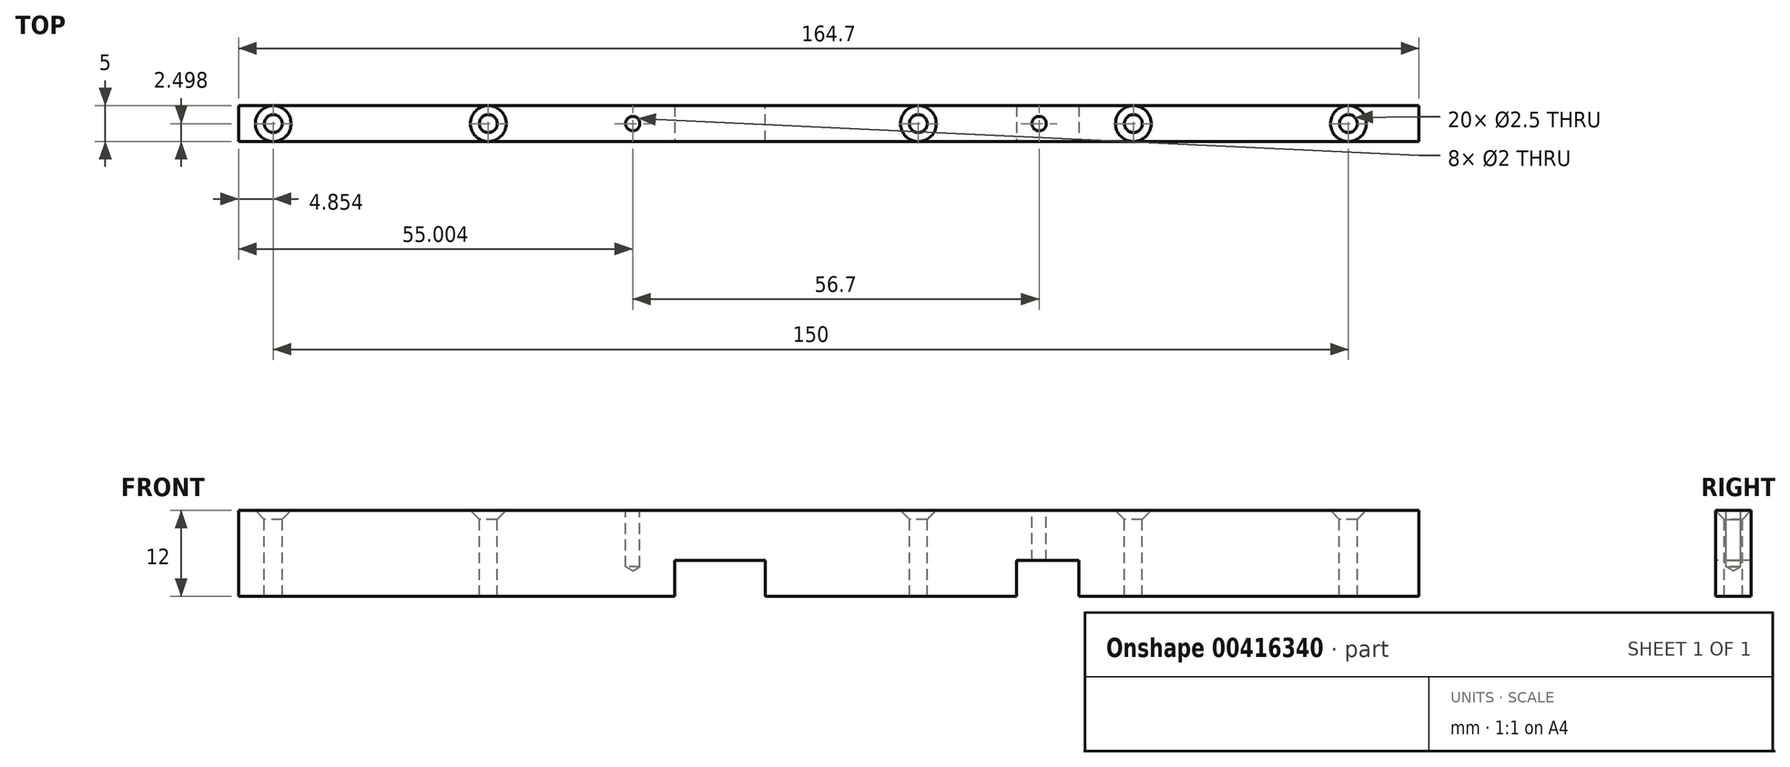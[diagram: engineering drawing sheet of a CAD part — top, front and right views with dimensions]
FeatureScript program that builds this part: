
annotation { "Feature Type Name" : "Feature", "Feature Type Description" : "" }
export const myFeature = defineFeature(function(context is Context, id is Id, definition is map)
    precondition{}
    {
        {
            var Q0;
            Q0=qCreatedBy(makeId("Top.planeOp"),FACE);
            var sketch = newSketch(context, id + "F0", { "sketchPlane" : qUnion([Q0])});
            skLineSegment(sketch, "E0", {"start": v(18.87, 90.14) * mm, "end": v(78.5, 90.14) * mm});
            skArc(sketch, "E1", {"start": v(18.87, 90.14) * mm, "mid": v(16.95, 89.76) * mm, "end": v(15.33, 88.67) * mm});
            skLineSegment(sketch, "E2", {"start": v(15.33, 88.67) * mm, "end": v(10.77, 84.1) * mm});
            skArc(sketch, "E3", {"start": v(10.77, 84.1) * mm, "mid": v(9.68, 82.49) * mm, "end": v(9.3, 80.57) * mm});
            skArc(sketch, "E4", {"start": v(15.33, 16.6) * mm, "mid": v(16.95, 15.52) * mm, "end": v(18.87, 15.14) * mm});
            skLineSegment(sketch, "E5", {"start": v(100.75, 15.14) * mm, "end": v(18.87, 15.14) * mm});
            skArc(sketch, "E6", {"start": v(100.75, 15.14) * mm, "mid": v(102.67, 15.52) * mm, "end": v(104.29, 16.6) * mm});
            skLineSegment(sketch, "E7", {"start": v(104.29, 16.6) * mm, "end": v(105.78, 18.1) * mm});
            skLineSegment(sketch, "E8", {"start": v(112.85, 18.1) * mm, "end": v(114.35, 16.6) * mm});
            skArc(sketch, "E9", {"start": v(114.35, 16.6) * mm, "mid": v(115.97, 15.52) * mm, "end": v(117.88, 15.14) * mm});
            skLineSegment(sketch, "E10", {"start": v(164.74, 15.14) * mm, "end": v(117.88, 15.14) * mm});
            skArc(sketch, "E11", {"start": v(164.74, 15.14) * mm, "mid": v(166.65, 15.52) * mm, "end": v(168.28, 16.6) * mm});
            skArc(sketch, "E12", {"start": v(172.84, 21.17) * mm, "mid": v(173.92, 22.79) * mm, "end": v(174.3, 24.7) * mm});
            skLineSegment(sketch, "E13", {"start": v(174.3, 80.57) * mm, "end": v(174.3, 24.7) * mm});
            skArc(sketch, "E14", {"start": v(174.3, 80.57) * mm, "mid": v(173.92, 82.49) * mm, "end": v(172.84, 84.1) * mm});
            skArc(sketch, "E15", {"start": v(168.28, 88.67) * mm, "mid": v(166.65, 89.76) * mm, "end": v(164.74, 90.14) * mm});
            skLineSegment(sketch, "E16", {"start": v(117.88, 90.14) * mm, "end": v(164.74, 90.14) * mm});
            skArc(sketch, "E17", {"start": v(117.88, 90.14) * mm, "mid": v(115.97, 89.76) * mm, "end": v(114.35, 88.67) * mm});
            skLineSegment(sketch, "E18", {"start": v(112.85, 87.18) * mm, "end": v(114.35, 88.67) * mm});
            skArc(sketch, "E19", {"start": v(105.78, 87.18) * mm, "mid": v(109.32, 85.72) * mm, "end": v(112.85, 87.18) * mm});
            skLineSegment(sketch, "E20", {"start": v(104.29, 88.67) * mm, "end": v(105.78, 87.18) * mm});
            skArc(sketch, "E21", {"start": v(104.29, 88.67) * mm, "mid": v(102.67, 89.76) * mm, "end": v(100.75, 90.14) * mm});
            skLineSegment(sketch, "E22", {"start": v(95.9, 90.14) * mm, "end": v(94.87, 91.17) * mm});
            skArc(sketch, "E23", {"start": v(91.33, 92.64) * mm, "mid": v(93.25, 92.26) * mm, "end": v(94.87, 91.17) * mm});
            skLineSegment(sketch, "E24", {"start": v(91.33, 92.64) * mm, "end": v(83.08, 92.64) * mm});
            skArc(sketch, "E25", {"start": v(79.54, 91.17) * mm, "mid": v(81.16, 92.26) * mm, "end": v(83.08, 92.64) * mm});
            skLineSegment(sketch, "E26", {"start": v(79.54, 91.17) * mm, "end": v(78.5, 90.14) * mm});
            skCircle(sketch, "E27", {"center": v(176.8, 54.89) * mm, "radius": 0.8 * mm});
            skCircle(sketch, "E28", {"center": v(176.8, 84.64) * mm, "radius": 0.8 * mm});
            skCircle(sketch, "E29", {"center": v(159.3, 12.64) * mm, "radius": 0.8 * mm});
            skCircle(sketch, "E30", {"center": v(176.8, 25.14) * mm, "radius": 0.8 * mm});
            skCircle(sketch, "E31", {"center": v(159.3, 92.64) * mm, "radius": 0.8 * mm});
            skCircle(sketch, "E32", {"center": v(119.3, 12.64) * mm, "radius": 0.8 * mm});
            skCircle(sketch, "E33", {"center": v(99.3, 12.64) * mm, "radius": 0.8 * mm});
            skCircle(sketch, "E34", {"center": v(59.3, 12.64) * mm, "radius": 0.8 * mm});
            skCircle(sketch, "E35", {"center": v(19.3, 12.64) * mm, "radius": 0.8 * mm});
            skCircle(sketch, "E36", {"center": v(119.3, 92.64) * mm, "radius": 0.8 * mm});
            skCircle(sketch, "E37", {"center": v(99.3, 92.64) * mm, "radius": 0.8 * mm});
            skCircle(sketch, "E38", {"center": v(6.8, 80.14) * mm, "radius": 0.8 * mm});
            skCircle(sketch, "E39", {"center": v(6.8, 53.84) * mm, "radius": 0.8 * mm});
            skCircle(sketch, "E40", {"center": v(59.3, 92.64) * mm, "radius": 0.8 * mm});
            skCircle(sketch, "E41", {"center": v(19.3, 92.64) * mm, "radius": 0.8 * mm});
            skLineSegment(sketch, "E42", {"start": v(4.3, 95.14) * mm, "end": v(179.3, 95.14) * mm});
            skLineSegment(sketch, "E43", {"start": v(179.3, 95.14) * mm, "end": v(179.3, 10.14) * mm});
            skLineSegment(sketch, "E44", {"start": v(179.3, 10.14) * mm, "end": v(4.3, 10.14) * mm});
            skCircle(sketch, "E45", {"center": v(9.3, 15.14) * mm, "radius": 2.15 * mm});
            skCircle(sketch, "E46", {"center": v(109.3, 15.14) * mm, "radius": 2.15 * mm});
            skCircle(sketch, "E47", {"center": v(9.3, 90.14) * mm, "radius": 2.15 * mm});
            skCircle(sketch, "E48", {"center": v(174.3, 90.14) * mm, "radius": 2.15 * mm});
            skCircle(sketch, "E49", {"center": v(174.3, 15.14) * mm, "radius": 2.15 * mm});
            skCircle(sketch, "E50", {"center": v(109.3, 90.14) * mm, "radius": 2.15 * mm});
            skLineSegment(sketch, "E51", {"start": v(95.9, 90.14) * mm, "end": v(100.75, 90.14) * mm});
            skArc(sketch, "E52", {"start": v(8.3, 25.7) * mm, "mid": v(8.68, 23.79) * mm, "end": v(9.77, 22.17) * mm});
            skArc(sketch, "E53", {"start": v(9.3, 49.78) * mm, "mid": v(8.56, 48.36) * mm, "end": v(8.3, 46.78) * mm});
            skLineSegment(sketch, "E54", {"start": v(9.3, 49.78) * mm, "end": v(9.3, 80.57) * mm});
            skLineSegment(sketch, "E55", {"start": v(15.33, 16.6) * mm, "end": v(9.77, 22.17) * mm});
            skLineSegment(sketch, "E56", {"start": v(8.3, 46.78) * mm, "end": v(8.3, 25.7) * mm});
            skLineSegment(sketch, "E57", {"start": v(168.28, 16.6) * mm, "end": v(172.84, 21.17) * mm});
            skLineSegment(sketch, "E58", {"start": v(4.3, 10.14) * mm, "end": v(4.3, 95.14) * mm});
            skLineSegment(sketch, "E59", {"start": v(168.28, 88.67) * mm, "end": v(172.84, 84.1) * mm});
            skLineSegment(sketch, "E60", {"start": v(9.3, 51.64) * mm, "end": v(9.8, 51.64) * mm});
            skLineSegment(sketch, "E61", {"start": v(9.8, 51.24) * mm, "end": v(9.3, 51.24) * mm});
            skLineSegment(sketch, "E62", {"start": v(9.34, 22.66) * mm, "end": v(9.8, 22.66) * mm});
            skArc(sketch, "E63", {"start": v(9.8, 23.9) * mm, "mid": v(11.41, 22.85) * mm, "end": v(13.3, 22.48) * mm});
            skLineSegment(sketch, "E64", {"start": v(13.3, 22.48) * mm, "end": v(124.3, 22.48) * mm});
            skArc(sketch, "E65", {"start": v(124.3, 22.48) * mm, "mid": v(127.84, 23.94) * mm, "end": v(129.3, 27.48) * mm});
            skLineSegment(sketch, "E66", {"start": v(129.3, 27.48) * mm, "end": v(129.3, 46.78) * mm});
            skArc(sketch, "E67", {"start": v(129.3, 46.78) * mm, "mid": v(127.84, 50.31) * mm, "end": v(124.3, 51.78) * mm});
            skLineSegment(sketch, "E68", {"start": v(13.3, 51.78) * mm, "end": v(124.3, 51.78) * mm});
            skArc(sketch, "E69", {"start": v(13.3, 51.78) * mm, "mid": v(11.41, 51.4) * mm, "end": v(9.8, 50.35) * mm});
            skLineSegment(sketch, "E70", {"start": v(9.8, 50.35) * mm, "end": v(9.8, 51.64) * mm});
            skLineSegment(sketch, "E71", {"start": v(9.8, 22.26) * mm, "end": v(9.8, 23.9) * mm});
            skLineSegment(sketch, "E72", {"start": v(36.43, 70.73) * mm, "end": v(36.43, 66.15) * mm});
            skLineSegment(sketch, "E73", {"start": v(36.43, 66.15) * mm, "end": v(23.24, 66.15) * mm});
            skArc(sketch, "E74", {"start": v(23.24, 66.15) * mm, "mid": v(18.24, 61.15) * mm, "end": v(23.24, 56.15) * mm});
            skLineSegment(sketch, "E75", {"start": v(63.42, 56.15) * mm, "end": v(23.24, 56.15) * mm});
            skArc(sketch, "E76", {"start": v(63.42, 56.15) * mm, "mid": v(66.95, 57.6) * mm, "end": v(68.42, 61.15) * mm});
            skLineSegment(sketch, "E77", {"start": v(68.42, 62.67) * mm, "end": v(68.42, 61.15) * mm});
            skArc(sketch, "E78", {"start": v(68.42, 62.67) * mm, "mid": v(66.95, 66.2) * mm, "end": v(63.42, 67.67) * mm});
            skLineSegment(sketch, "E79", {"start": v(58.94, 67.67) * mm, "end": v(63.42, 67.67) * mm});
            skLineSegment(sketch, "E80", {"start": v(58.94, 70.73) * mm, "end": v(58.94, 67.67) * mm});
            skArc(sketch, "E81", {"start": v(58.94, 70.73) * mm, "mid": v(57.47, 74.27) * mm, "end": v(53.94, 75.73) * mm});
            skLineSegment(sketch, "E82", {"start": v(41.43, 75.73) * mm, "end": v(53.94, 75.73) * mm});
            skArc(sketch, "E83", {"start": v(41.43, 75.73) * mm, "mid": v(37.9, 74.27) * mm, "end": v(36.43, 70.73) * mm});
            skCircle(sketch, "E84", {"center": v(20.67, 88.22) * mm, "radius": 1.5 * mm});
            skCircle(sketch, "E85", {"center": v(43.43, 88.22) * mm, "radius": 1.5 * mm});
            skCircle(sketch, "E86", {"center": v(87.18, 87.32) * mm, "radius": 1.02 * mm});
            skCircle(sketch, "E87", {"center": v(87.19, 66.74) * mm, "radius": 1.02 * mm});
            skCircle(sketch, "E88", {"center": v(12.43, 67.14) * mm, "radius": 0.8 * mm});
            skCircle(sketch, "E89", {"center": v(24.3, 72.14) * mm, "radius": 0.8 * mm});
            skCircle(sketch, "E90", {"center": v(25.95, 86.94) * mm, "radius": 0.8 * mm});
            skCircle(sketch, "E91", {"center": v(56.3, 87.03) * mm, "radius": 0.8 * mm});
            skCircle(sketch, "E92", {"center": v(61.25, 73.02) * mm, "radius": 0.8 * mm});
            skCircle(sketch, "E93", {"center": v(77.3, 87.03) * mm, "radius": 0.8 * mm});
            skCircle(sketch, "E94", {"center": v(103.58, 71.9) * mm, "radius": 0.8 * mm});
            skCircle(sketch, "E95", {"center": v(95.44, 87.66) * mm, "radius": 0.8 * mm});
            skCircle(sketch, "E96", {"center": v(112.81, 82.14) * mm, "radius": 0.8 * mm});
            skCircle(sketch, "E97", {"center": v(132.3, 71.14) * mm, "radius": 0.8 * mm});
            skCircle(sketch, "E98", {"center": v(131.08, 84.74) * mm, "radius": 0.8 * mm});
            skCircle(sketch, "E99", {"center": v(148.41, 39.7) * mm, "radius": 0.8 * mm});
            skCircle(sketch, "E100", {"center": v(170.3, 28.14) * mm, "radius": 0.8 * mm});
            skCircle(sketch, "E101", {"center": v(169.46, 82.57) * mm, "radius": 0.8 * mm});
            skCircle(sketch, "E102", {"center": v(171.43, 70.95) * mm, "radius": 0.8 * mm});
            skCircle(sketch, "E103", {"center": v(79.53, 66.84) * mm, "radius": 0.8 * mm});
            skCircle(sketch, "E104", {"center": v(158.16, 71.12) * mm, "radius": 0.8 * mm});
            skCircle(sketch, "E105", {"center": v(158.22, 82.82) * mm, "radius": 0.8 * mm});
            skLineSegment(sketch, "E106", {"start": v(153.8, 58.09) * mm, "end": v(137, 58.09) * mm});
            skArc(sketch, "E107", {"start": v(155.3, 59.59) * mm, "mid": v(154.86, 58.53) * mm, "end": v(153.8, 58.09) * mm});
            skLineSegment(sketch, "E108", {"start": v(155.3, 83.2) * mm, "end": v(155.3, 59.59) * mm});
            skArc(sketch, "E109", {"start": v(153.8, 84.7) * mm, "mid": v(154.86, 84.25) * mm, "end": v(155.3, 83.2) * mm});
            skLineSegment(sketch, "E110", {"start": v(137, 84.7) * mm, "end": v(153.8, 84.7) * mm});
            skArc(sketch, "E111", {"start": v(135.5, 83.2) * mm, "mid": v(135.93, 84.25) * mm, "end": v(137, 84.7) * mm});
            skLineSegment(sketch, "E112", {"start": v(135.5, 59.59) * mm, "end": v(135.5, 83.2) * mm});
            skArc(sketch, "E113", {"start": v(137, 58.09) * mm, "mid": v(135.93, 58.53) * mm, "end": v(135.5, 59.59) * mm});
            skArc(sketch, "E114", {"start": v(9.8, 23.9) * mm, "mid": v(8.7, 25.54) * mm, "end": v(8.3, 27.48) * mm});
            skArc(sketch, "E115", {"start": v(9.3, 49.78) * mm, "mid": v(9.54, 50.07) * mm, "end": v(9.8, 50.35) * mm});
            skLineSegment(sketch, "E116", {"start": v(18.3, 27.48) * mm, "end": v(18.3, 46.78) * mm});
            skArc(sketch, "E117", {"start": v(13.3, 22.48) * mm, "mid": v(16.84, 23.94) * mm, "end": v(18.3, 27.48) * mm});
            skArc(sketch, "E118", {"start": v(18.3, 46.78) * mm, "mid": v(16.84, 50.31) * mm, "end": v(13.3, 51.78) * mm});
            skCircle(sketch, "E119", {"center": v(152.55, 66.64) * mm, "radius": 0.6 * mm});
            skCircle(sketch, "E120", {"center": v(152.55, 81.14) * mm, "radius": 0.6 * mm});
            skCircle(sketch, "E121", {"center": v(138.05, 66.64) * mm, "radius": 0.6 * mm});
            skCircle(sketch, "E122", {"center": v(138.05, 81.14) * mm, "radius": 0.6 * mm});
            skCircle(sketch, "E123", {"center": v(19.3, 92.64) * mm, "radius": 0.78 * mm});
            skArc(sketch, "E124", {"start": v(19.1, 91.66) * mm, "mid": v(20.02, 93.33) * mm, "end": v(18.32, 92.47) * mm});
            skCircle(sketch, "E125", {"center": v(25.95, 86.94) * mm, "radius": 0.78 * mm});
            skArc(sketch, "E126", {"start": v(25.76, 85.96) * mm, "mid": v(26.67, 87.63) * mm, "end": v(24.97, 86.77) * mm});
            skCircle(sketch, "E127", {"center": v(6.8, 80.14) * mm, "radius": 0.78 * mm});
            skArc(sketch, "E128", {"start": v(6.6, 79.16) * mm, "mid": v(7.52, 80.83) * mm, "end": v(5.82, 79.97) * mm});
            skCircle(sketch, "E129", {"center": v(24.3, 72.14) * mm, "radius": 0.78 * mm});
            skArc(sketch, "E130", {"start": v(24.1, 71.16) * mm, "mid": v(25.02, 72.83) * mm, "end": v(23.32, 71.97) * mm});
            skCircle(sketch, "E131", {"center": v(12.43, 67.14) * mm, "radius": 0.78 * mm});
            skArc(sketch, "E132", {"start": v(12.23, 66.16) * mm, "mid": v(13.14, 67.83) * mm, "end": v(11.44, 66.97) * mm});
            skCircle(sketch, "E133", {"center": v(59.3, 92.64) * mm, "radius": 0.78 * mm});
            skArc(sketch, "E134", {"start": v(59.1, 91.66) * mm, "mid": v(60.02, 93.33) * mm, "end": v(58.32, 92.47) * mm});
            skCircle(sketch, "E135", {"center": v(56.3, 87.03) * mm, "radius": 0.78 * mm});
            skArc(sketch, "E136", {"start": v(56.1, 86.05) * mm, "mid": v(57.02, 87.73) * mm, "end": v(55.32, 86.87) * mm});
            skCircle(sketch, "E137", {"center": v(77.3, 87.03) * mm, "radius": 0.78 * mm});
            skArc(sketch, "E138", {"start": v(77.1, 86.05) * mm, "mid": v(78.02, 87.73) * mm, "end": v(76.32, 86.87) * mm});
            skCircle(sketch, "E139", {"center": v(61.25, 73.02) * mm, "radius": 0.78 * mm});
            skArc(sketch, "E140", {"start": v(61.06, 72.04) * mm, "mid": v(61.97, 73.71) * mm, "end": v(60.27, 72.85) * mm});
            skCircle(sketch, "E141", {"center": v(99.3, 92.64) * mm, "radius": 0.78 * mm});
            skArc(sketch, "E142", {"start": v(99.1, 91.66) * mm, "mid": v(100.02, 93.33) * mm, "end": v(98.32, 92.47) * mm});
            skCircle(sketch, "E143", {"center": v(95.44, 87.66) * mm, "radius": 0.78 * mm});
            skArc(sketch, "E144", {"start": v(95.25, 86.68) * mm, "mid": v(96.16, 88.36) * mm, "end": v(94.46, 87.5) * mm});
            skCircle(sketch, "E145", {"center": v(103.58, 71.9) * mm, "radius": 0.78 * mm});
            skArc(sketch, "E146", {"start": v(103.39, 70.92) * mm, "mid": v(104.3, 72.6) * mm, "end": v(102.6, 71.73) * mm});
            skCircle(sketch, "E147", {"center": v(79.53, 66.84) * mm, "radius": 0.78 * mm});
            skArc(sketch, "E148", {"start": v(79.33, 65.86) * mm, "mid": v(80.25, 67.54) * mm, "end": v(78.54, 66.68) * mm});
            skCircle(sketch, "E149", {"center": v(119.3, 92.64) * mm, "radius": 0.78 * mm});
            skArc(sketch, "E150", {"start": v(119.1, 91.66) * mm, "mid": v(120.02, 93.33) * mm, "end": v(118.32, 92.47) * mm});
            skCircle(sketch, "E151", {"center": v(131.08, 84.74) * mm, "radius": 0.78 * mm});
            skArc(sketch, "E152", {"start": v(130.89, 83.76) * mm, "mid": v(131.8, 85.43) * mm, "end": v(130.1, 84.57) * mm});
            skCircle(sketch, "E153", {"center": v(132.3, 71.14) * mm, "radius": 0.78 * mm});
            skArc(sketch, "E154", {"start": v(132.1, 70.16) * mm, "mid": v(133.02, 71.83) * mm, "end": v(131.32, 70.97) * mm});
            skCircle(sketch, "E155", {"center": v(159.3, 92.64) * mm, "radius": 0.78 * mm});
            skArc(sketch, "E156", {"start": v(159.1, 91.66) * mm, "mid": v(160.02, 93.33) * mm, "end": v(158.32, 92.47) * mm});
            skCircle(sketch, "E157", {"center": v(158.22, 82.82) * mm, "radius": 0.78 * mm});
            skArc(sketch, "E158", {"start": v(158.03, 81.84) * mm, "mid": v(158.94, 83.51) * mm, "end": v(157.24, 82.65) * mm});
            skCircle(sketch, "E159", {"center": v(158.16, 71.12) * mm, "radius": 0.78 * mm});
            skArc(sketch, "E160", {"start": v(157.97, 70.14) * mm, "mid": v(158.88, 71.81) * mm, "end": v(157.18, 70.95) * mm});
            skCircle(sketch, "E161", {"center": v(169.46, 82.57) * mm, "radius": 0.78 * mm});
            skArc(sketch, "E162", {"start": v(169.27, 81.59) * mm, "mid": v(170.18, 83.26) * mm, "end": v(168.48, 82.4) * mm});
            skCircle(sketch, "E163", {"center": v(171.43, 70.95) * mm, "radius": 0.78 * mm});
            skArc(sketch, "E164", {"start": v(171.24, 69.97) * mm, "mid": v(172.15, 71.64) * mm, "end": v(170.45, 70.78) * mm});
            skCircle(sketch, "E165", {"center": v(176.8, 84.64) * mm, "radius": 0.78 * mm});
            skArc(sketch, "E166", {"start": v(176.6, 83.66) * mm, "mid": v(177.52, 85.33) * mm, "end": v(175.82, 84.47) * mm});
            skCircle(sketch, "E167", {"center": v(176.8, 54.89) * mm, "radius": 0.78 * mm});
            skArc(sketch, "E168", {"start": v(176.6, 53.9) * mm, "mid": v(177.52, 55.58) * mm, "end": v(175.82, 54.72) * mm});
            skCircle(sketch, "E169", {"center": v(176.8, 25.14) * mm, "radius": 0.78 * mm});
            skArc(sketch, "E170", {"start": v(176.6, 24.16) * mm, "mid": v(177.52, 25.83) * mm, "end": v(175.82, 24.97) * mm});
            skCircle(sketch, "E171", {"center": v(170.3, 28.14) * mm, "radius": 0.78 * mm});
            skArc(sketch, "E172", {"start": v(170.1, 27.16) * mm, "mid": v(171.02, 28.83) * mm, "end": v(169.32, 27.97) * mm});
            skCircle(sketch, "E173", {"center": v(148.41, 39.7) * mm, "radius": 0.78 * mm});
            skArc(sketch, "E174", {"start": v(148.22, 38.71) * mm, "mid": v(149.13, 40.4) * mm, "end": v(147.43, 39.53) * mm});
            skCircle(sketch, "E175", {"center": v(159.3, 12.64) * mm, "radius": 0.78 * mm});
            skArc(sketch, "E176", {"start": v(159.1, 11.66) * mm, "mid": v(160.02, 13.33) * mm, "end": v(158.32, 12.47) * mm});
            skCircle(sketch, "E177", {"center": v(164.3, 53.64) * mm, "radius": 0.78 * mm});
            skCircle(sketch, "E178", {"center": v(134.3, 53.64) * mm, "radius": 0.78 * mm});
            skCircle(sketch, "E179", {"center": v(104.3, 53.64) * mm, "radius": 0.78 * mm});
            skCircle(sketch, "E180", {"center": v(99.3, 12.64) * mm, "radius": 0.78 * mm});
            skArc(sketch, "E181", {"start": v(99.1, 11.66) * mm, "mid": v(100.02, 13.33) * mm, "end": v(98.32, 12.47) * mm});
            skCircle(sketch, "E182", {"center": v(119.3, 12.64) * mm, "radius": 0.78 * mm});
            skArc(sketch, "E183", {"start": v(119.1, 11.66) * mm, "mid": v(120.02, 13.33) * mm, "end": v(118.32, 12.47) * mm});
            skCircle(sketch, "E184", {"center": v(74.3, 53.64) * mm, "radius": 0.78 * mm});
            skCircle(sketch, "E185", {"center": v(59.3, 12.64) * mm, "radius": 0.78 * mm});
            skArc(sketch, "E186", {"start": v(59.1, 11.66) * mm, "mid": v(60.02, 13.33) * mm, "end": v(58.32, 12.47) * mm});
            skCircle(sketch, "E187", {"center": v(19.3, 12.64) * mm, "radius": 0.78 * mm});
            skArc(sketch, "E188", {"start": v(19.1, 11.66) * mm, "mid": v(20.02, 13.33) * mm, "end": v(18.32, 12.47) * mm});
            skCircle(sketch, "E189", {"center": v(6.8, 53.84) * mm, "radius": 0.78 * mm});
            skArc(sketch, "E190", {"start": v(6.6, 52.86) * mm, "mid": v(7.52, 54.53) * mm, "end": v(5.82, 53.67) * mm});
            skCircle(sketch, "E191", {"center": v(14.3, 53.64) * mm, "radius": 0.78 * mm});
            skCircle(sketch, "E192", {"center": v(44.3, 53.64) * mm, "radius": 0.78 * mm});
            skArc(sketch, "E193", {"start": v(86.86, 86.1) * mm, "mid": v(88.07, 88.2) * mm, "end": v(85.98, 87) * mm});
            skArc(sketch, "E194", {"start": v(86.86, 65.53) * mm, "mid": v(88.07, 67.63) * mm, "end": v(85.98, 66.42) * mm});
            skCircle(sketch, "E195", {"center": v(138.05, 81.14) * mm, "radius": 1.02 * mm});
            skArc(sketch, "E196", {"start": v(137.72, 79.93) * mm, "mid": v(138.93, 82.02) * mm, "end": v(136.84, 80.81) * mm});
            skCircle(sketch, "E197", {"center": v(152.55, 81.14) * mm, "radius": 1.02 * mm});
            skArc(sketch, "E198", {"start": v(152.22, 79.93) * mm, "mid": v(153.43, 82.02) * mm, "end": v(151.34, 80.81) * mm});
            skCircle(sketch, "E199", {"center": v(152.55, 66.64) * mm, "radius": 1.02 * mm});
            skArc(sketch, "E200", {"start": v(152.22, 65.43) * mm, "mid": v(153.43, 67.52) * mm, "end": v(151.34, 66.31) * mm});
            skCircle(sketch, "E201", {"center": v(138.05, 66.64) * mm, "radius": 1.02 * mm});
            skArc(sketch, "E202", {"start": v(137.72, 65.43) * mm, "mid": v(138.93, 67.52) * mm, "end": v(136.84, 66.31) * mm});
            skArc(sketch, "E203", {"start": v(112.62, 81.16) * mm, "mid": v(113.53, 82.83) * mm, "end": v(111.83, 81.97) * mm});
            skLineSegment(sketch, "E204", {"start": v(9.45, 51.14) * mm, "end": v(9.45, 56.14) * mm});
            skLineSegment(sketch, "E205", {"start": v(9.45, 56.14) * mm, "end": v(70.3, 56.14) * mm});
            skLineSegment(sketch, "E206", {"start": v(70.3, 56.14) * mm, "end": v(70.3, 51.14) * mm});
            skLineSegment(sketch, "E207", {"start": v(70.3, 51.14) * mm, "end": v(9.45, 51.14) * mm});
            skLineSegment(sketch, "E208", {"start": v(82.98, 51.14) * mm, "end": v(82.98, 56.14) * mm});
            skLineSegment(sketch, "E209", {"start": v(82.98, 56.14) * mm, "end": v(117.98, 56.14) * mm});
            skLineSegment(sketch, "E210", {"start": v(117.98, 56.14) * mm, "end": v(117.98, 51.14) * mm});
            skLineSegment(sketch, "E211", {"start": v(117.98, 51.14) * mm, "end": v(82.98, 51.14) * mm});
            skLineSegment(sketch, "E212", {"start": v(174.15, 51.14) * mm, "end": v(174.15, 56.14) * mm});
            skLineSegment(sketch, "E213", {"start": v(174.15, 56.14) * mm, "end": v(126.7, 56.14) * mm});
            skLineSegment(sketch, "E214", {"start": v(126.7, 56.14) * mm, "end": v(126.7, 51.14) * mm});
            skLineSegment(sketch, "E215", {"start": v(126.7, 51.14) * mm, "end": v(174.15, 51.14) * mm});
            skLineSegment(sketch, "E216", {"start": v(70.3, 51.14) * mm, "end": v(82.98, 51.14) * mm});
            skLineSegment(sketch, "E217", {"start": v(82.98, 56.14) * mm, "end": v(70.3, 56.14) * mm});
            skLineSegment(sketch, "E218", {"start": v(126.7, 51.14) * mm, "end": v(126.7, 56.14) * mm});
            skLineSegment(sketch, "E219", {"start": v(126.7, 56.14) * mm, "end": v(117.98, 56.14) * mm});
            skLineSegment(sketch, "E220", {"start": v(117.98, 51.14) * mm, "end": v(126.7, 51.14) * mm});
            skSolve(sketch);
        }
        {
            var Q0;
            Q0=makeQuery(id+"F0.imprint","IMPRINT",FACE,{"disambiguationData":[TD([[makeQuery(id+"F0.imprint","IMPRINT",EDGE,{"derivedFrom":sQuery(id+"F0.wireOp",EDGE,"E191")}),1.0]])]});
            var Q1;
            {var subQ1=sQuery(id+"F0.wireOp",EDGE,"E69");var subQ3=sQuery(id+"F0.wireOp",EDGE,"E207");var subQ4=makeQuery(id+"F0.imprint","INTERSECT",VERTEX,{"derivedFrom":[subQ1,subQ3]});Q1=makeQuery(id+"F0.imprint","IMPRINT",FACE,{"disambiguationData":[TD([[makeQuery(id+"F0.imprint","IMPRINT",EDGE,{"disambiguationData":[TD([[subQ4,1.0]])],"derivedFrom":subQ3}),-1.0]])]});}
            var Q2;
            {var subQ1=sQuery(id+"F0.wireOp",EDGE,"E68");var subQ3=sQuery(id+"F0.wireOp",EDGE,"E206");var subQ4=makeQuery(id+"F0.imprint","INTERSECT",VERTEX,{"derivedFrom":[subQ1,subQ3]});Q2=makeQuery(id+"F0.imprint","IMPRINT",FACE,{"disambiguationData":[TD([[makeQuery(id+"F0.imprint","IMPRINT",EDGE,{"disambiguationData":[TD([[subQ4,1.0]])],"derivedFrom":subQ1}),-1.0]])]});}
            var Q3;
            {var subQ0=sQuery(id+"F0.wireOp",EDGE,"E70");var subQ1=sQuery(id+"F0.wireOp",EDGE,"E60");var subQ2=makeQuery(id+"F0.imprint","INTERSECT",VERTEX,{"derivedFrom":[subQ1,subQ0]});Q3=makeQuery(id+"F0.imprint","IMPRINT",FACE,{"disambiguationData":[TD([[makeQuery(id+"F0.imprint","IMPRINT",EDGE,{"disambiguationData":[TD([[subQ2,1.0]])],"derivedFrom":subQ1}),-1.0]])]});}
            var Q4;
            {var subQ0=sQuery(id+"F0.wireOp",EDGE,"E70");var subQ1=sQuery(id+"F0.wireOp",EDGE,"E61");var subQ2=makeQuery(id+"F0.imprint","INTERSECT",VERTEX,{"derivedFrom":[subQ1,subQ0]});Q4=makeQuery(id+"F0.imprint","IMPRINT",FACE,{"disambiguationData":[TD([[makeQuery(id+"F0.imprint","IMPRINT",EDGE,{"disambiguationData":[TD([[subQ2,-1.0]])],"derivedFrom":subQ1}),1.0]])]});}
            var Q5;
            Q5=makeQuery(id+"F0.imprint","IMPRINT",FACE,{"disambiguationData":[TD([[makeQuery(id+"F0.imprint","IMPRINT",EDGE,{"derivedFrom":sQuery(id+"F0.wireOp",EDGE,"E179")}),1.0]])]});
            var Q6;
            {var subQ5=sQuery(id+"F0.wireOp",EDGE,"E216");Q6=makeQuery(id+"F0.imprint","IMPRINT",FACE,{"disambiguationData":[TD([[makeQuery(id+"F0.imprint","IMPRINT",EDGE,{"derivedFrom":subQ5}),1.0]])]});}
            var Q7;
            {var subQ5=sQuery(id+"F0.wireOp",EDGE,"E211");Q7=makeQuery(id+"F0.imprint","IMPRINT",FACE,{"disambiguationData":[TD([[makeQuery(id+"F0.imprint","IMPRINT",EDGE,{"derivedFrom":subQ5}),-1.0]])]});}
            var Q8;
            Q8=makeQuery(id+"F0.imprint","IMPRINT",FACE,{"disambiguationData":[TD([[makeQuery(id+"F0.imprint","IMPRINT",EDGE,{"derivedFrom":sQuery(id+"F0.wireOp",EDGE,"E177")}),1.0]])]});
            var Q9;
            {var subQ0=sQuery(id+"F0.wireOp",EDGE,"E215");var subQ1=sQuery(id+"F0.wireOp",EDGE,"E67");var subQ2=makeQuery(id+"F0.imprint","INTERSECT",VERTEX,{"derivedFrom":[subQ1,subQ0]});Q9=makeQuery(id+"F0.imprint","IMPRINT",FACE,{"disambiguationData":[TD([[makeQuery(id+"F0.imprint","IMPRINT",EDGE,{"disambiguationData":[TD([[subQ2,-1.0]])],"derivedFrom":subQ1}),1.0]])]});}
            var Q10;
            {var subQ0=sQuery(id+"F0.wireOp",EDGE,"E220");Q10=makeQuery(id+"F0.imprint","IMPRINT",FACE,{"disambiguationData":[TD([[makeQuery(id+"F0.imprint","IMPRINT",EDGE,{"derivedFrom":subQ0}),1.0]])]});}
            var Q11;
            Q11=makeQuery(id+"F0.imprint","IMPRINT",FACE,{"disambiguationData":[TD([[makeQuery(id+"F0.imprint","IMPRINT",EDGE,{"derivedFrom":sQuery(id+"F0.wireOp",EDGE,"E184")}),1.0]])]});
            var Q12;
            {var subQ0=sQuery(id+"F0.wireOp",EDGE,"E219");Q12=makeQuery(id+"F0.imprint","IMPRINT",FACE,{"disambiguationData":[TD([[makeQuery(id+"F0.imprint","IMPRINT",EDGE,{"derivedFrom":subQ0}),1.0]])]});}
            var Q13;
            Q13=makeQuery(id+"F0.imprint","IMPRINT",FACE,{"disambiguationData":[TD([[makeQuery(id+"F0.imprint","IMPRINT",EDGE,{"derivedFrom":sQuery(id+"F0.wireOp",EDGE,"E191")}),-1.0]])]});
            var Q14;
            Q14=makeQuery(id+"F0.imprint","IMPRINT",FACE,{"disambiguationData":[TD([[makeQuery(id+"F0.imprint","IMPRINT",EDGE,{"derivedFrom":sQuery(id+"F0.wireOp",EDGE,"E192")}),-1.0]])]});
            var Q15;
            Q15=makeQuery(id+"F0.imprint","IMPRINT",FACE,{"disambiguationData":[TD([[makeQuery(id+"F0.imprint","IMPRINT",EDGE,{"derivedFrom":sQuery(id+"F0.wireOp",EDGE,"E184")}),-1.0]])]});
            var Q16;
            Q16=makeQuery(id+"F0.imprint","IMPRINT",FACE,{"disambiguationData":[TD([[makeQuery(id+"F0.imprint","IMPRINT",EDGE,{"derivedFrom":sQuery(id+"F0.wireOp",EDGE,"E179")}),-1.0]])]});
            var Q17;
            Q17=makeQuery(id+"F0.imprint","IMPRINT",FACE,{"disambiguationData":[TD([[makeQuery(id+"F0.imprint","IMPRINT",EDGE,{"derivedFrom":sQuery(id+"F0.wireOp",EDGE,"E178")}),-1.0]])]});
            var Q18;
            Q18=makeQuery(id+"F0.imprint","IMPRINT",FACE,{"disambiguationData":[TD([[makeQuery(id+"F0.imprint","IMPRINT",EDGE,{"derivedFrom":sQuery(id+"F0.wireOp",EDGE,"E177")}),-1.0]])]});
            extrude(context, id + "F1", {"entities" : qUnion([Q0, Q1, Q2, Q3, Q4, Q5, Q6, Q7, Q8, Q9, Q10, Q11, Q12, Q13, Q14, Q15, Q16, Q17, Q18]), "depth" : 12 * mm, "offsetDistance" : 25 * mm});
        }
        {
            var Q0;
            Q0=makeQuery(id+"F1.opExtrude","CAP_FACE",FACE,{"disambiguationData":[OSD([sQuery(id+"F0.wireOp",EDGE,"E177"),sQuery(id+"F0.wireOp",EDGE,"E178"),sQuery(id+"F0.wireOp",EDGE,"E179"),sQuery(id+"F0.wireOp",EDGE,"E184"),sQuery(id+"F0.wireOp",EDGE,"E191"),sQuery(id+"F0.wireOp",EDGE,"E192"),sQuery(id+"F0.wireOp",EDGE,"E204"),sQuery(id+"F0.wireOp",EDGE,"E205"),sQuery(id+"F0.wireOp",EDGE,"E207"),sQuery(id+"F0.wireOp",EDGE,"E209"),sQuery(id+"F0.wireOp",EDGE,"E211"),sQuery(id+"F0.wireOp",EDGE,"E212"),sQuery(id+"F0.wireOp",EDGE,"E213"),sQuery(id+"F0.wireOp",EDGE,"E215"),sQuery(id+"F0.wireOp",EDGE,"E216"),sQuery(id+"F0.wireOp",EDGE,"E217"),sQuery(id+"F0.wireOp",EDGE,"E219"),sQuery(id+"F0.wireOp",EDGE,"E220")])],"isStart":false});
            var sketch = newSketch(context, id + "F2", { "sketchPlane" : qUnion([Q0])});
            skLineSegment(sketch, "E221", {"start": v(18.87, 90.14) * mm, "end": v(78.5, 90.14) * mm});
            skArc(sketch, "E222", {"start": v(18.87, 90.14) * mm, "mid": v(16.95, 89.76) * mm, "end": v(15.33, 88.67) * mm});
            skLineSegment(sketch, "E223", {"start": v(15.33, 88.67) * mm, "end": v(10.77, 84.1) * mm});
            skArc(sketch, "E224", {"start": v(10.77, 84.1) * mm, "mid": v(9.68, 82.49) * mm, "end": v(9.3, 80.57) * mm});
            skArc(sketch, "E225", {"start": v(15.33, 16.6) * mm, "mid": v(16.95, 15.52) * mm, "end": v(18.87, 15.14) * mm});
            skLineSegment(sketch, "E226", {"start": v(100.75, 15.14) * mm, "end": v(18.87, 15.14) * mm});
            skArc(sketch, "E227", {"start": v(100.75, 15.14) * mm, "mid": v(102.67, 15.52) * mm, "end": v(104.29, 16.6) * mm});
            skLineSegment(sketch, "E228", {"start": v(104.29, 16.6) * mm, "end": v(105.78, 18.1) * mm});
            skLineSegment(sketch, "E229", {"start": v(112.85, 18.1) * mm, "end": v(114.35, 16.6) * mm});
            skArc(sketch, "E230", {"start": v(114.35, 16.6) * mm, "mid": v(115.97, 15.52) * mm, "end": v(117.88, 15.14) * mm});
            skLineSegment(sketch, "E231", {"start": v(164.74, 15.14) * mm, "end": v(117.88, 15.14) * mm});
            skArc(sketch, "E232", {"start": v(164.74, 15.14) * mm, "mid": v(166.65, 15.52) * mm, "end": v(168.28, 16.6) * mm});
            skArc(sketch, "E233", {"start": v(172.84, 21.17) * mm, "mid": v(173.92, 22.79) * mm, "end": v(174.3, 24.7) * mm});
            skLineSegment(sketch, "E234", {"start": v(174.3, 80.57) * mm, "end": v(174.3, 24.7) * mm});
            skArc(sketch, "E235", {"start": v(174.3, 80.57) * mm, "mid": v(173.92, 82.49) * mm, "end": v(172.84, 84.1) * mm});
            skArc(sketch, "E236", {"start": v(168.28, 88.67) * mm, "mid": v(166.65, 89.76) * mm, "end": v(164.74, 90.14) * mm});
            skLineSegment(sketch, "E237", {"start": v(117.88, 90.14) * mm, "end": v(164.74, 90.14) * mm});
            skArc(sketch, "E238", {"start": v(117.88, 90.14) * mm, "mid": v(115.97, 89.76) * mm, "end": v(114.35, 88.67) * mm});
            skLineSegment(sketch, "E239", {"start": v(112.85, 87.18) * mm, "end": v(114.35, 88.67) * mm});
            skArc(sketch, "E240", {"start": v(105.78, 87.18) * mm, "mid": v(109.32, 85.72) * mm, "end": v(112.85, 87.18) * mm});
            skLineSegment(sketch, "E241", {"start": v(104.29, 88.67) * mm, "end": v(105.78, 87.18) * mm});
            skArc(sketch, "E242", {"start": v(104.29, 88.67) * mm, "mid": v(102.67, 89.76) * mm, "end": v(100.75, 90.14) * mm});
            skLineSegment(sketch, "E243", {"start": v(95.9, 90.14) * mm, "end": v(94.87, 91.17) * mm});
            skArc(sketch, "E244", {"start": v(91.33, 92.64) * mm, "mid": v(93.25, 92.26) * mm, "end": v(94.87, 91.17) * mm});
            skLineSegment(sketch, "E245", {"start": v(91.33, 92.64) * mm, "end": v(83.08, 92.64) * mm});
            skArc(sketch, "E246", {"start": v(79.54, 91.17) * mm, "mid": v(81.16, 92.26) * mm, "end": v(83.08, 92.64) * mm});
            skLineSegment(sketch, "E247", {"start": v(79.54, 91.17) * mm, "end": v(78.5, 90.14) * mm});
            skCircle(sketch, "E248", {"center": v(176.8, 54.89) * mm, "radius": 0.8 * mm});
            skCircle(sketch, "E249", {"center": v(176.8, 84.64) * mm, "radius": 0.8 * mm});
            skCircle(sketch, "E250", {"center": v(159.3, 12.64) * mm, "radius": 0.8 * mm});
            skCircle(sketch, "E251", {"center": v(176.8, 25.14) * mm, "radius": 0.8 * mm});
            skCircle(sketch, "E252", {"center": v(159.3, 92.64) * mm, "radius": 0.8 * mm});
            skCircle(sketch, "E253", {"center": v(119.3, 12.64) * mm, "radius": 0.8 * mm});
            skCircle(sketch, "E254", {"center": v(99.3, 12.64) * mm, "radius": 0.8 * mm});
            skCircle(sketch, "E255", {"center": v(59.3, 12.64) * mm, "radius": 0.8 * mm});
            skCircle(sketch, "E256", {"center": v(19.3, 12.64) * mm, "radius": 0.8 * mm});
            skCircle(sketch, "E257", {"center": v(119.3, 92.64) * mm, "radius": 0.8 * mm});
            skCircle(sketch, "E258", {"center": v(99.3, 92.64) * mm, "radius": 0.8 * mm});
            skCircle(sketch, "E259", {"center": v(6.8, 80.14) * mm, "radius": 0.8 * mm});
            skCircle(sketch, "E260", {"center": v(6.8, 53.84) * mm, "radius": 0.8 * mm});
            skCircle(sketch, "E261", {"center": v(59.3, 92.64) * mm, "radius": 0.8 * mm});
            skCircle(sketch, "E262", {"center": v(19.3, 92.64) * mm, "radius": 0.8 * mm});
            skLineSegment(sketch, "E263", {"start": v(4.3, 95.14) * mm, "end": v(179.3, 95.14) * mm});
            skLineSegment(sketch, "E264", {"start": v(179.3, 95.14) * mm, "end": v(179.3, 10.14) * mm});
            skLineSegment(sketch, "E265", {"start": v(179.3, 10.14) * mm, "end": v(4.3, 10.14) * mm});
            skCircle(sketch, "E266", {"center": v(9.3, 15.14) * mm, "radius": 2.15 * mm});
            skCircle(sketch, "E267", {"center": v(109.3, 15.14) * mm, "radius": 2.15 * mm});
            skCircle(sketch, "E268", {"center": v(9.3, 90.14) * mm, "radius": 2.15 * mm});
            skCircle(sketch, "E269", {"center": v(174.3, 90.14) * mm, "radius": 2.15 * mm});
            skCircle(sketch, "E270", {"center": v(174.3, 15.14) * mm, "radius": 2.15 * mm});
            skCircle(sketch, "E271", {"center": v(109.3, 90.14) * mm, "radius": 2.15 * mm});
            skLineSegment(sketch, "E272", {"start": v(95.9, 90.14) * mm, "end": v(100.75, 90.14) * mm});
            skArc(sketch, "E273", {"start": v(8.3, 25.7) * mm, "mid": v(8.68, 23.79) * mm, "end": v(9.77, 22.17) * mm});
            skArc(sketch, "E274", {"start": v(9.3, 49.78) * mm, "mid": v(8.56, 48.36) * mm, "end": v(8.3, 46.78) * mm});
            skLineSegment(sketch, "E275", {"start": v(9.3, 49.78) * mm, "end": v(9.3, 80.57) * mm});
            skLineSegment(sketch, "E276", {"start": v(15.33, 16.6) * mm, "end": v(9.77, 22.17) * mm});
            skLineSegment(sketch, "E277", {"start": v(8.3, 46.78) * mm, "end": v(8.3, 25.7) * mm});
            skLineSegment(sketch, "E278", {"start": v(168.28, 16.6) * mm, "end": v(172.84, 21.17) * mm});
            skLineSegment(sketch, "E279", {"start": v(4.3, 10.14) * mm, "end": v(4.3, 95.14) * mm});
            skLineSegment(sketch, "E280", {"start": v(168.28, 88.67) * mm, "end": v(172.84, 84.1) * mm});
            skLineSegment(sketch, "E281", {"start": v(9.3, 51.64) * mm, "end": v(9.8, 51.64) * mm});
            skLineSegment(sketch, "E282", {"start": v(9.8, 51.24) * mm, "end": v(9.3, 51.24) * mm});
            skLineSegment(sketch, "E283", {"start": v(9.34, 22.66) * mm, "end": v(9.8, 22.66) * mm});
            skArc(sketch, "E284", {"start": v(9.8, 23.9) * mm, "mid": v(11.41, 22.85) * mm, "end": v(13.3, 22.48) * mm});
            skLineSegment(sketch, "E285", {"start": v(13.3, 22.48) * mm, "end": v(124.3, 22.48) * mm});
            skArc(sketch, "E286", {"start": v(124.3, 22.48) * mm, "mid": v(127.84, 23.94) * mm, "end": v(129.3, 27.48) * mm});
            skLineSegment(sketch, "E287", {"start": v(129.3, 27.48) * mm, "end": v(129.3, 46.78) * mm});
            skArc(sketch, "E288", {"start": v(129.3, 46.78) * mm, "mid": v(127.84, 50.31) * mm, "end": v(124.3, 51.78) * mm});
            skLineSegment(sketch, "E289", {"start": v(13.3, 51.78) * mm, "end": v(124.3, 51.78) * mm});
            skArc(sketch, "E290", {"start": v(13.3, 51.78) * mm, "mid": v(11.41, 51.4) * mm, "end": v(9.8, 50.35) * mm});
            skLineSegment(sketch, "E291", {"start": v(9.8, 50.35) * mm, "end": v(9.8, 51.64) * mm});
            skLineSegment(sketch, "E292", {"start": v(9.8, 22.26) * mm, "end": v(9.8, 23.9) * mm});
            skLineSegment(sketch, "E293", {"start": v(36.43, 70.73) * mm, "end": v(36.43, 66.15) * mm});
            skLineSegment(sketch, "E294", {"start": v(36.43, 66.15) * mm, "end": v(23.24, 66.15) * mm});
            skArc(sketch, "E295", {"start": v(23.24, 66.15) * mm, "mid": v(18.24, 61.15) * mm, "end": v(23.24, 56.15) * mm});
            skLineSegment(sketch, "E296", {"start": v(63.42, 56.15) * mm, "end": v(23.24, 56.15) * mm});
            skArc(sketch, "E297", {"start": v(63.42, 56.15) * mm, "mid": v(66.95, 57.6) * mm, "end": v(68.42, 61.15) * mm});
            skLineSegment(sketch, "E298", {"start": v(68.42, 62.67) * mm, "end": v(68.42, 61.15) * mm});
            skArc(sketch, "E299", {"start": v(68.42, 62.67) * mm, "mid": v(66.95, 66.2) * mm, "end": v(63.42, 67.67) * mm});
            skLineSegment(sketch, "E300", {"start": v(58.94, 67.67) * mm, "end": v(63.42, 67.67) * mm});
            skLineSegment(sketch, "E301", {"start": v(58.94, 70.73) * mm, "end": v(58.94, 67.67) * mm});
            skArc(sketch, "E302", {"start": v(58.94, 70.73) * mm, "mid": v(57.47, 74.27) * mm, "end": v(53.94, 75.73) * mm});
            skLineSegment(sketch, "E303", {"start": v(41.43, 75.73) * mm, "end": v(53.94, 75.73) * mm});
            skArc(sketch, "E304", {"start": v(41.43, 75.73) * mm, "mid": v(37.9, 74.27) * mm, "end": v(36.43, 70.73) * mm});
            skCircle(sketch, "E305", {"center": v(20.67, 88.22) * mm, "radius": 1.5 * mm});
            skCircle(sketch, "E306", {"center": v(43.43, 88.22) * mm, "radius": 1.5 * mm});
            skCircle(sketch, "E307", {"center": v(87.18, 87.32) * mm, "radius": 1.02 * mm});
            skCircle(sketch, "E308", {"center": v(87.19, 66.74) * mm, "radius": 1.02 * mm});
            skCircle(sketch, "E309", {"center": v(12.43, 67.14) * mm, "radius": 0.8 * mm});
            skCircle(sketch, "E310", {"center": v(24.3, 72.14) * mm, "radius": 0.8 * mm});
            skCircle(sketch, "E311", {"center": v(25.95, 86.94) * mm, "radius": 0.8 * mm});
            skCircle(sketch, "E312", {"center": v(56.3, 87.03) * mm, "radius": 0.8 * mm});
            skCircle(sketch, "E313", {"center": v(61.25, 73.02) * mm, "radius": 0.8 * mm});
            skCircle(sketch, "E314", {"center": v(77.3, 87.03) * mm, "radius": 0.8 * mm});
            skCircle(sketch, "E315", {"center": v(103.58, 71.9) * mm, "radius": 0.8 * mm});
            skCircle(sketch, "E316", {"center": v(95.44, 87.66) * mm, "radius": 0.8 * mm});
            skCircle(sketch, "E317", {"center": v(112.81, 82.14) * mm, "radius": 0.8 * mm});
            skCircle(sketch, "E318", {"center": v(132.3, 71.14) * mm, "radius": 0.8 * mm});
            skCircle(sketch, "E319", {"center": v(131.08, 84.74) * mm, "radius": 0.8 * mm});
            skCircle(sketch, "E320", {"center": v(148.41, 39.7) * mm, "radius": 0.8 * mm});
            skCircle(sketch, "E321", {"center": v(170.3, 28.14) * mm, "radius": 0.8 * mm});
            skCircle(sketch, "E322", {"center": v(169.46, 82.57) * mm, "radius": 0.8 * mm});
            skCircle(sketch, "E323", {"center": v(171.43, 70.95) * mm, "radius": 0.8 * mm});
            skCircle(sketch, "E324", {"center": v(79.53, 66.84) * mm, "radius": 0.8 * mm});
            skCircle(sketch, "E325", {"center": v(158.16, 71.12) * mm, "radius": 0.8 * mm});
            skCircle(sketch, "E326", {"center": v(158.22, 82.82) * mm, "radius": 0.8 * mm});
            skLineSegment(sketch, "E327", {"start": v(153.8, 58.09) * mm, "end": v(137, 58.09) * mm});
            skArc(sketch, "E328", {"start": v(155.3, 59.59) * mm, "mid": v(154.86, 58.53) * mm, "end": v(153.8, 58.09) * mm});
            skLineSegment(sketch, "E329", {"start": v(155.3, 83.2) * mm, "end": v(155.3, 59.59) * mm});
            skArc(sketch, "E330", {"start": v(153.8, 84.7) * mm, "mid": v(154.86, 84.25) * mm, "end": v(155.3, 83.2) * mm});
            skLineSegment(sketch, "E331", {"start": v(137, 84.7) * mm, "end": v(153.8, 84.7) * mm});
            skArc(sketch, "E332", {"start": v(135.5, 83.2) * mm, "mid": v(135.93, 84.25) * mm, "end": v(137, 84.7) * mm});
            skLineSegment(sketch, "E333", {"start": v(135.5, 59.59) * mm, "end": v(135.5, 83.2) * mm});
            skArc(sketch, "E334", {"start": v(137, 58.09) * mm, "mid": v(135.93, 58.53) * mm, "end": v(135.5, 59.59) * mm});
            skArc(sketch, "E335", {"start": v(9.8, 23.9) * mm, "mid": v(8.7, 25.54) * mm, "end": v(8.3, 27.48) * mm});
            skArc(sketch, "E336", {"start": v(9.3, 49.78) * mm, "mid": v(9.54, 50.07) * mm, "end": v(9.8, 50.35) * mm});
            skLineSegment(sketch, "E337", {"start": v(18.3, 27.48) * mm, "end": v(18.3, 46.78) * mm});
            skArc(sketch, "E338", {"start": v(13.3, 22.48) * mm, "mid": v(16.84, 23.94) * mm, "end": v(18.3, 27.48) * mm});
            skArc(sketch, "E339", {"start": v(18.3, 46.78) * mm, "mid": v(16.84, 50.31) * mm, "end": v(13.3, 51.78) * mm});
            skCircle(sketch, "E340", {"center": v(152.55, 66.64) * mm, "radius": 0.6 * mm});
            skCircle(sketch, "E341", {"center": v(152.55, 81.14) * mm, "radius": 0.6 * mm});
            skCircle(sketch, "E342", {"center": v(138.05, 66.64) * mm, "radius": 0.6 * mm});
            skCircle(sketch, "E343", {"center": v(138.05, 81.14) * mm, "radius": 0.6 * mm});
            skCircle(sketch, "E344", {"center": v(19.3, 92.64) * mm, "radius": 0.78 * mm});
            skArc(sketch, "E345", {"start": v(19.1, 91.66) * mm, "mid": v(20.02, 93.33) * mm, "end": v(18.32, 92.47) * mm});
            skCircle(sketch, "E346", {"center": v(25.95, 86.94) * mm, "radius": 0.78 * mm});
            skArc(sketch, "E347", {"start": v(25.76, 85.96) * mm, "mid": v(26.67, 87.63) * mm, "end": v(24.97, 86.77) * mm});
            skCircle(sketch, "E348", {"center": v(6.8, 80.14) * mm, "radius": 0.78 * mm});
            skArc(sketch, "E349", {"start": v(6.6, 79.16) * mm, "mid": v(7.52, 80.83) * mm, "end": v(5.82, 79.97) * mm});
            skCircle(sketch, "E350", {"center": v(24.3, 72.14) * mm, "radius": 0.78 * mm});
            skArc(sketch, "E351", {"start": v(24.1, 71.16) * mm, "mid": v(25.02, 72.83) * mm, "end": v(23.32, 71.97) * mm});
            skCircle(sketch, "E352", {"center": v(12.43, 67.14) * mm, "radius": 0.78 * mm});
            skArc(sketch, "E353", {"start": v(12.23, 66.16) * mm, "mid": v(13.14, 67.83) * mm, "end": v(11.44, 66.97) * mm});
            skCircle(sketch, "E354", {"center": v(59.3, 92.64) * mm, "radius": 0.78 * mm});
            skArc(sketch, "E355", {"start": v(59.1, 91.66) * mm, "mid": v(60.02, 93.33) * mm, "end": v(58.32, 92.47) * mm});
            skCircle(sketch, "E356", {"center": v(56.3, 87.03) * mm, "radius": 0.78 * mm});
            skArc(sketch, "E357", {"start": v(56.1, 86.05) * mm, "mid": v(57.02, 87.73) * mm, "end": v(55.32, 86.87) * mm});
            skCircle(sketch, "E358", {"center": v(77.3, 87.03) * mm, "radius": 0.78 * mm});
            skArc(sketch, "E359", {"start": v(77.1, 86.05) * mm, "mid": v(78.02, 87.73) * mm, "end": v(76.32, 86.87) * mm});
            skCircle(sketch, "E360", {"center": v(61.25, 73.02) * mm, "radius": 0.78 * mm});
            skArc(sketch, "E361", {"start": v(61.06, 72.04) * mm, "mid": v(61.97, 73.71) * mm, "end": v(60.27, 72.85) * mm});
            skCircle(sketch, "E362", {"center": v(99.3, 92.64) * mm, "radius": 0.78 * mm});
            skArc(sketch, "E363", {"start": v(99.1, 91.66) * mm, "mid": v(100.02, 93.33) * mm, "end": v(98.32, 92.47) * mm});
            skCircle(sketch, "E364", {"center": v(95.44, 87.66) * mm, "radius": 0.78 * mm});
            skArc(sketch, "E365", {"start": v(95.25, 86.68) * mm, "mid": v(96.16, 88.36) * mm, "end": v(94.46, 87.5) * mm});
            skCircle(sketch, "E366", {"center": v(103.58, 71.9) * mm, "radius": 0.78 * mm});
            skArc(sketch, "E367", {"start": v(103.39, 70.92) * mm, "mid": v(104.3, 72.6) * mm, "end": v(102.6, 71.73) * mm});
            skCircle(sketch, "E368", {"center": v(79.53, 66.84) * mm, "radius": 0.78 * mm});
            skArc(sketch, "E369", {"start": v(79.33, 65.86) * mm, "mid": v(80.25, 67.54) * mm, "end": v(78.54, 66.68) * mm});
            skCircle(sketch, "E370", {"center": v(119.3, 92.64) * mm, "radius": 0.78 * mm});
            skArc(sketch, "E371", {"start": v(119.1, 91.66) * mm, "mid": v(120.02, 93.33) * mm, "end": v(118.32, 92.47) * mm});
            skCircle(sketch, "E372", {"center": v(131.08, 84.74) * mm, "radius": 0.78 * mm});
            skArc(sketch, "E373", {"start": v(130.89, 83.76) * mm, "mid": v(131.8, 85.43) * mm, "end": v(130.1, 84.57) * mm});
            skCircle(sketch, "E374", {"center": v(132.3, 71.14) * mm, "radius": 0.78 * mm});
            skArc(sketch, "E375", {"start": v(132.1, 70.16) * mm, "mid": v(133.02, 71.83) * mm, "end": v(131.32, 70.97) * mm});
            skCircle(sketch, "E376", {"center": v(159.3, 92.64) * mm, "radius": 0.78 * mm});
            skArc(sketch, "E377", {"start": v(159.1, 91.66) * mm, "mid": v(160.02, 93.33) * mm, "end": v(158.32, 92.47) * mm});
            skCircle(sketch, "E378", {"center": v(158.22, 82.82) * mm, "radius": 0.78 * mm});
            skArc(sketch, "E379", {"start": v(158.03, 81.84) * mm, "mid": v(158.94, 83.51) * mm, "end": v(157.24, 82.65) * mm});
            skCircle(sketch, "E380", {"center": v(158.16, 71.12) * mm, "radius": 0.78 * mm});
            skArc(sketch, "E381", {"start": v(157.97, 70.14) * mm, "mid": v(158.88, 71.81) * mm, "end": v(157.18, 70.95) * mm});
            skCircle(sketch, "E382", {"center": v(169.46, 82.57) * mm, "radius": 0.78 * mm});
            skArc(sketch, "E383", {"start": v(169.27, 81.59) * mm, "mid": v(170.18, 83.26) * mm, "end": v(168.48, 82.4) * mm});
            skCircle(sketch, "E384", {"center": v(171.43, 70.95) * mm, "radius": 0.78 * mm});
            skArc(sketch, "E385", {"start": v(171.24, 69.97) * mm, "mid": v(172.15, 71.64) * mm, "end": v(170.45, 70.78) * mm});
            skCircle(sketch, "E386", {"center": v(176.8, 84.64) * mm, "radius": 0.78 * mm});
            skArc(sketch, "E387", {"start": v(176.6, 83.66) * mm, "mid": v(177.52, 85.33) * mm, "end": v(175.82, 84.47) * mm});
            skCircle(sketch, "E388", {"center": v(176.8, 54.89) * mm, "radius": 0.78 * mm});
            skArc(sketch, "E389", {"start": v(176.6, 53.9) * mm, "mid": v(177.52, 55.58) * mm, "end": v(175.82, 54.72) * mm});
            skCircle(sketch, "E390", {"center": v(176.8, 25.14) * mm, "radius": 0.78 * mm});
            skArc(sketch, "E391", {"start": v(176.6, 24.16) * mm, "mid": v(177.52, 25.83) * mm, "end": v(175.82, 24.97) * mm});
            skCircle(sketch, "E392", {"center": v(170.3, 28.14) * mm, "radius": 0.78 * mm});
            skArc(sketch, "E393", {"start": v(170.1, 27.16) * mm, "mid": v(171.02, 28.83) * mm, "end": v(169.32, 27.97) * mm});
            skCircle(sketch, "E394", {"center": v(148.41, 39.7) * mm, "radius": 0.78 * mm});
            skArc(sketch, "E395", {"start": v(148.22, 38.71) * mm, "mid": v(149.13, 40.4) * mm, "end": v(147.43, 39.53) * mm});
            skCircle(sketch, "E396", {"center": v(159.3, 12.64) * mm, "radius": 0.78 * mm});
            skArc(sketch, "E397", {"start": v(159.1, 11.66) * mm, "mid": v(160.02, 13.33) * mm, "end": v(158.32, 12.47) * mm});
            skCircle(sketch, "E398", {"center": v(164.3, 53.64) * mm, "radius": 0.78 * mm});
            skCircle(sketch, "E399", {"center": v(134.3, 53.64) * mm, "radius": 0.78 * mm});
            skCircle(sketch, "E400", {"center": v(104.3, 53.64) * mm, "radius": 0.78 * mm});
            skCircle(sketch, "E401", {"center": v(99.3, 12.64) * mm, "radius": 0.78 * mm});
            skArc(sketch, "E402", {"start": v(99.1, 11.66) * mm, "mid": v(100.02, 13.33) * mm, "end": v(98.32, 12.47) * mm});
            skCircle(sketch, "E403", {"center": v(119.3, 12.64) * mm, "radius": 0.78 * mm});
            skArc(sketch, "E404", {"start": v(119.1, 11.66) * mm, "mid": v(120.02, 13.33) * mm, "end": v(118.32, 12.47) * mm});
            skCircle(sketch, "E405", {"center": v(74.3, 53.64) * mm, "radius": 0.78 * mm});
            skCircle(sketch, "E406", {"center": v(59.3, 12.64) * mm, "radius": 0.78 * mm});
            skArc(sketch, "E407", {"start": v(59.1, 11.66) * mm, "mid": v(60.02, 13.33) * mm, "end": v(58.32, 12.47) * mm});
            skCircle(sketch, "E408", {"center": v(19.3, 12.64) * mm, "radius": 0.78 * mm});
            skArc(sketch, "E409", {"start": v(19.1, 11.66) * mm, "mid": v(20.02, 13.33) * mm, "end": v(18.32, 12.47) * mm});
            skCircle(sketch, "E410", {"center": v(6.8, 53.84) * mm, "radius": 0.78 * mm});
            skArc(sketch, "E411", {"start": v(6.6, 52.86) * mm, "mid": v(7.52, 54.53) * mm, "end": v(5.82, 53.67) * mm});
            skCircle(sketch, "E412", {"center": v(14.3, 53.64) * mm, "radius": 0.78 * mm});
            skCircle(sketch, "E413", {"center": v(44.3, 53.64) * mm, "radius": 0.78 * mm});
            skArc(sketch, "E414", {"start": v(86.86, 86.1) * mm, "mid": v(88.07, 88.2) * mm, "end": v(85.98, 87) * mm});
            skArc(sketch, "E415", {"start": v(86.86, 65.53) * mm, "mid": v(88.07, 67.63) * mm, "end": v(85.98, 66.42) * mm});
            skCircle(sketch, "E416", {"center": v(138.05, 81.14) * mm, "radius": 1.02 * mm});
            skArc(sketch, "E417", {"start": v(137.72, 79.93) * mm, "mid": v(138.93, 82.02) * mm, "end": v(136.84, 80.81) * mm});
            skCircle(sketch, "E418", {"center": v(152.55, 81.14) * mm, "radius": 1.02 * mm});
            skArc(sketch, "E419", {"start": v(152.22, 79.93) * mm, "mid": v(153.43, 82.02) * mm, "end": v(151.34, 80.81) * mm});
            skCircle(sketch, "E420", {"center": v(152.55, 66.64) * mm, "radius": 1.02 * mm});
            skArc(sketch, "E421", {"start": v(152.22, 65.43) * mm, "mid": v(153.43, 67.52) * mm, "end": v(151.34, 66.31) * mm});
            skCircle(sketch, "E422", {"center": v(138.05, 66.64) * mm, "radius": 1.02 * mm});
            skArc(sketch, "E423", {"start": v(137.72, 65.43) * mm, "mid": v(138.93, 67.52) * mm, "end": v(136.84, 66.31) * mm});
            skArc(sketch, "E424", {"start": v(112.62, 81.16) * mm, "mid": v(113.53, 82.83) * mm, "end": v(111.83, 81.97) * mm});
            skLineSegment(sketch, "E425", {"start": v(9.45, 51.14) * mm, "end": v(9.45, 56.14) * mm});
            skLineSegment(sketch, "E426", {"start": v(9.45, 56.14) * mm, "end": v(70.3, 56.14) * mm});
            skLineSegment(sketch, "E427", {"start": v(70.3, 56.14) * mm, "end": v(70.3, 51.14) * mm});
            skLineSegment(sketch, "E428", {"start": v(70.3, 51.14) * mm, "end": v(9.45, 51.14) * mm});
            skLineSegment(sketch, "E429", {"start": v(82.98, 51.14) * mm, "end": v(82.98, 56.14) * mm});
            skLineSegment(sketch, "E430", {"start": v(82.98, 56.14) * mm, "end": v(117.98, 56.14) * mm});
            skLineSegment(sketch, "E431", {"start": v(117.98, 56.14) * mm, "end": v(117.98, 51.14) * mm});
            skLineSegment(sketch, "E432", {"start": v(117.98, 51.14) * mm, "end": v(82.98, 51.14) * mm});
            skLineSegment(sketch, "E433", {"start": v(174.15, 51.14) * mm, "end": v(174.15, 56.14) * mm});
            skLineSegment(sketch, "E434", {"start": v(174.15, 56.14) * mm, "end": v(126.7, 56.14) * mm});
            skLineSegment(sketch, "E435", {"start": v(126.7, 56.14) * mm, "end": v(126.7, 51.14) * mm});
            skLineSegment(sketch, "E436", {"start": v(126.7, 51.14) * mm, "end": v(174.15, 51.14) * mm});
            skLineSegment(sketch, "E437", {"start": v(70.3, 51.14) * mm, "end": v(82.98, 51.14) * mm});
            skLineSegment(sketch, "E438", {"start": v(82.98, 56.14) * mm, "end": v(70.3, 56.14) * mm});
            skLineSegment(sketch, "E439", {"start": v(126.7, 51.14) * mm, "end": v(126.7, 56.14) * mm});
            skLineSegment(sketch, "E440", {"start": v(126.7, 56.14) * mm, "end": v(117.98, 56.14) * mm});
            skLineSegment(sketch, "E441", {"start": v(117.98, 51.14) * mm, "end": v(126.7, 51.14) * mm});
            skCircle(sketch, "E442", {"center": v(64.45, 53.64) * mm, "radius": 1.15 * mm});
            skCircle(sketch, "E443", {"center": v(121.15, 53.64) * mm, "radius": 1 * mm});
            skSolve(sketch);
        }
        {
            var Q0;
            Q0=sQuery(id+"F2.wireOp",VERTEX,"E412.center");
            var Q1;
            Q1=sQuery(id+"F2.wireOp",VERTEX,"E413.center");
            var Q2;
            Q2=sQuery(id+"F2.wireOp",VERTEX,"E400.center");
            var Q3;
            Q3=sQuery(id+"F2.wireOp",VERTEX,"E399.center");
            var Q4;
            Q4=sQuery(id+"F2.wireOp",VERTEX,"E398.center");
            var Q5;
            Q5=makeQuery(id+"F1.opExtrude","SWEPT_BODY",BODY,{"disambiguationData":[OSD([sQuery(id+"F0.wireOp",EDGE,"E204"),sQuery(id+"F0.wireOp",EDGE,"E205"),sQuery(id+"F0.wireOp",EDGE,"E207"),sQuery(id+"F0.wireOp",EDGE,"E209"),sQuery(id+"F0.wireOp",EDGE,"E211"),sQuery(id+"F0.wireOp",EDGE,"E212"),sQuery(id+"F0.wireOp",EDGE,"E213"),sQuery(id+"F0.wireOp",EDGE,"E215"),sQuery(id+"F0.wireOp",EDGE,"E216"),sQuery(id+"F0.wireOp",EDGE,"E217"),sQuery(id+"F0.wireOp",EDGE,"E219"),sQuery(id+"F0.wireOp",EDGE,"E220")])]});
            hole(context, id + "F3", {"style" : HoleStyle.C_SINK, "endStyle" : HoleEndStyle.THROUGH, "holeDiameter" : 2.5 * mm, "cSinkDiameter" : 5 * mm, "cSinkAngle" : 90 * degree, "tappedDepth" : 12 * mm, "tapClearance" : 3, "locations" : qUnion([Q0, Q1, Q2, Q3, Q4]), "scope" : qUnion([Q5])});
        }
        {
            var Q0;
            Q0=makeQuery(id+"F0.imprint","IMPRINT",FACE,{"disambiguationData":[TD([[makeQuery(id+"F0.imprint","IMPRINT",EDGE,{"derivedFrom":sQuery(id+"F0.wireOp",EDGE,"E184")}),1.0]])]});
            var Q1;
            {var subQ5=sQuery(id+"F0.wireOp",EDGE,"E216");Q1=makeQuery(id+"F0.imprint","IMPRINT",FACE,{"disambiguationData":[TD([[makeQuery(id+"F0.imprint","IMPRINT",EDGE,{"derivedFrom":subQ5}),1.0]])]});}
            var Q2;
            {var subQ0=sQuery(id+"F0.wireOp",EDGE,"E219");Q2=makeQuery(id+"F0.imprint","IMPRINT",FACE,{"disambiguationData":[TD([[makeQuery(id+"F0.imprint","IMPRINT",EDGE,{"derivedFrom":subQ0}),1.0]])]});}
            var Q3;
            {var subQ0=sQuery(id+"F0.wireOp",EDGE,"E220");Q3=makeQuery(id+"F0.imprint","IMPRINT",FACE,{"disambiguationData":[TD([[makeQuery(id+"F0.imprint","IMPRINT",EDGE,{"derivedFrom":subQ0}),1.0]])]});}
            var Q4;
            Q4=makeQuery(id+"F0.imprint","IMPRINT",FACE,{"disambiguationData":[TD([[makeQuery(id+"F0.imprint","IMPRINT",EDGE,{"derivedFrom":sQuery(id+"F0.wireOp",EDGE,"E184")}),-1.0]])]});
            extrude(context, id + "F4", {"entities" : qUnion([Q0, Q1, Q2, Q3, Q4]), "operationType" : NewBodyOperationType.REMOVE, "depth" : 5 * mm});
        }
        {
            var Q0;
            Q0=makeQuery(id+"F1.opExtrude","SWEPT_FACE",FACE,{"disambiguationData":[OSD([sQuery(id+"F0.wireOp",EDGE,"E212")])]});
            extrude(context, id + "F5", {"entities" : qUnion([Q0]), "depth" : 25 * mm, "offsetDistance" : 25 * mm});
        }
        {
            var Q0;
            Q0=sQuery(id+"F2.wireOp",VERTEX,"E248.center");
            var Q1;
            Q1=makeQuery(id+"F5.opExtrude","SWEPT_BODY",BODY,{"disambiguationData":[OSD([sQuery(id+"F0.wireOp",EDGE,"E212")])]});
            var Q2;
            Q2=makeQuery(id+"F1.opExtrude","SWEPT_BODY",BODY,{"disambiguationData":[OSD([sQuery(id+"F0.wireOp",EDGE,"E204"),sQuery(id+"F0.wireOp",EDGE,"E205"),sQuery(id+"F0.wireOp",EDGE,"E207"),sQuery(id+"F0.wireOp",EDGE,"E209"),sQuery(id+"F0.wireOp",EDGE,"E211"),sQuery(id+"F0.wireOp",EDGE,"E212"),sQuery(id+"F0.wireOp",EDGE,"E213"),sQuery(id+"F0.wireOp",EDGE,"E215"),sQuery(id+"F0.wireOp",EDGE,"E216"),sQuery(id+"F0.wireOp",EDGE,"E217"),sQuery(id+"F0.wireOp",EDGE,"E219"),sQuery(id+"F0.wireOp",EDGE,"E220")])]});
            hole(context, id + "F6", {"style" : HoleStyle.SIMPLE, "endStyle" : HoleEndStyle.BLIND, "holeDiameter" : 2 * mm, "majorDiameter" : 5 * mm, "holeDepth" : 5.5 * mm, "tappedDepth" : 12 * mm, "tapClearance" : 3, "locations" : qUnion([Q0]), "scope" : qUnion([Q1, Q2])});
        }
        {
            var Q0;
            {var subQ0=makeQuery(id+"F3.hole-1.opRevolve","SWEPT_FACE",FACE,{"disambiguationData":[OSD([sQuery(id+"F3.hole-1.sketch.wireOp",EDGE,"csink_start_line_1")])]});var subQ1=sQuery(id+"F0.wireOp",EDGE,"E220");var subQ2=sQuery(id+"F0.wireOp",EDGE,"E216");var subQ3=sQuery(id+"F0.wireOp",EDGE,"E215");var subQ4=sQuery(id+"F0.wireOp",EDGE,"E211");var subQ5=sQuery(id+"F0.wireOp",EDGE,"E207");var subQ7=sQuery(id+"F0.wireOp",EDGE,"E219");var subQ8=sQuery(id+"F0.wireOp",EDGE,"E217");var subQ9=sQuery(id+"F0.wireOp",EDGE,"E213");var subQ10=sQuery(id+"F0.wireOp",EDGE,"E209");var subQ11=sQuery(id+"F0.wireOp",EDGE,"E205");var subQ13=sQuery(id+"F0.wireOp",EDGE,"E212");var subQ14=makeQuery(id+"F1.opExtrude","CAP_FACE",FACE,{"disambiguationData":[OSD([sQuery(id+"F0.wireOp",EDGE,"E204"),subQ11,subQ5,subQ10,subQ4,subQ13,subQ9,subQ3,subQ2,subQ8,subQ7,subQ1])],"isStart":false});var subQ15=makeQuery(id+"F1.opExtrude","SWEPT_FACE",FACE,{"disambiguationData":[OSD([subQ13])]});Q0=makeQuery(id+"F3.hole-2.boolean.opBoolean","SPLIT",FACE,{"disambiguationData":[TD([makeQuery(id+"F3.hole-1.boolean.opBoolean","COPY",FACE,{"derivedFrom":subQ0})])],"derivedFrom":makeQuery(id+"F3.hole-1.boolean.opBoolean","SPLIT",FACE,{"disambiguationData":[TD([subQ15])],"derivedFrom":makeQuery(id+"F3.hole-0.boolean.opBoolean","SPLIT",FACE,{"disambiguationData":[TD([subQ15])],"derivedFrom":subQ14})})});}
            extrude(context, id + "F7", {"entities" : qUnion([Q0]), "oppositeDirection" : true, "depth" : 12 * mm, "offsetDistance" : 25 * mm});
        }
        {
            var Q0;
            Q0=sQuery(id+"F2.wireOp",VERTEX,"E442.center");
            var Q1;
            Q1=makeQuery(id+"F1.opExtrude","SWEPT_BODY",BODY,{"disambiguationData":[OSD([sQuery(id+"F0.wireOp",EDGE,"E204"),sQuery(id+"F0.wireOp",EDGE,"E205"),sQuery(id+"F0.wireOp",EDGE,"E207"),sQuery(id+"F0.wireOp",EDGE,"E209"),sQuery(id+"F0.wireOp",EDGE,"E211"),sQuery(id+"F0.wireOp",EDGE,"E212"),sQuery(id+"F0.wireOp",EDGE,"E213"),sQuery(id+"F0.wireOp",EDGE,"E215"),sQuery(id+"F0.wireOp",EDGE,"E216"),sQuery(id+"F0.wireOp",EDGE,"E217"),sQuery(id+"F0.wireOp",EDGE,"E219"),sQuery(id+"F0.wireOp",EDGE,"E220")])]});
            var Q2;
            Q2=makeQuery(id+"F7.opExtrude","SWEPT_BODY",BODY,{"disambiguationData":[OSD([sQuery(id+"F0.wireOp",EDGE,"E204"),sQuery(id+"F0.wireOp",EDGE,"E205"),sQuery(id+"F0.wireOp",EDGE,"E207"),sQuery(id+"F0.wireOp",EDGE,"E209"),sQuery(id+"F0.wireOp",EDGE,"E211"),sQuery(id+"F0.wireOp",EDGE,"E212"),sQuery(id+"F0.wireOp",EDGE,"E213"),sQuery(id+"F0.wireOp",EDGE,"E215"),sQuery(id+"F0.wireOp",EDGE,"E216"),sQuery(id+"F0.wireOp",EDGE,"E217"),sQuery(id+"F0.wireOp",EDGE,"E219"),sQuery(id+"F0.wireOp",EDGE,"E220")])]});
            hole(context, id + "F8", {"style" : HoleStyle.SIMPLE, "endStyle" : HoleEndStyle.BLIND_IN_LAST, "holeDiameter" : 2 * mm, "tapDrillDiameter" : 1.6 * mm, "majorDiameter" : 5 * mm, "holeDepth" : 8 * mm, "tappedDepth" : 12 * mm, "tapClearance" : 3, "locations" : qUnion([Q0]), "scope" : qUnion([Q1, Q2])});
        }
        {
            var Q0;
            Q0=makeQuery(id+"F5.opExtrude","SWEPT_BODY",BODY,{"disambiguationData":[OSD([sQuery(id+"F0.wireOp",EDGE,"E212")])]});
            deleteBodies(context, id + "F9", {"entities" : qUnion([Q0])});
        }
        {
            var Q0;
            Q0=makeQuery(id+"F7.opExtrude","SWEPT_BODY",BODY,{"disambiguationData":[OSD([sQuery(id+"F0.wireOp",EDGE,"E204"),sQuery(id+"F0.wireOp",EDGE,"E205"),sQuery(id+"F0.wireOp",EDGE,"E207"),sQuery(id+"F0.wireOp",EDGE,"E209"),sQuery(id+"F0.wireOp",EDGE,"E211"),sQuery(id+"F0.wireOp",EDGE,"E212"),sQuery(id+"F0.wireOp",EDGE,"E213"),sQuery(id+"F0.wireOp",EDGE,"E215"),sQuery(id+"F0.wireOp",EDGE,"E216"),sQuery(id+"F0.wireOp",EDGE,"E217"),sQuery(id+"F0.wireOp",EDGE,"E219"),sQuery(id+"F0.wireOp",EDGE,"E220")])]});
            deleteBodies(context, id + "F10", {"entities" : qUnion([Q0])});
        }
        {
            var Q0;
            {var subQ0=makeQuery(id+"F3.hole-2.opRevolve","SWEPT_FACE",FACE,{"disambiguationData":[OSD([sQuery(id+"F3.hole-2.sketch.wireOp",EDGE,"csink_start_line_1")])]});var subQ1=sQuery(id+"F0.wireOp",EDGE,"E220");var subQ2=sQuery(id+"F0.wireOp",EDGE,"E216");var subQ3=sQuery(id+"F0.wireOp",EDGE,"E215");var subQ4=sQuery(id+"F0.wireOp",EDGE,"E211");var subQ5=sQuery(id+"F0.wireOp",EDGE,"E207");var subQ7=sQuery(id+"F0.wireOp",EDGE,"E219");var subQ8=sQuery(id+"F0.wireOp",EDGE,"E217");var subQ9=sQuery(id+"F0.wireOp",EDGE,"E213");var subQ10=sQuery(id+"F0.wireOp",EDGE,"E209");var subQ11=sQuery(id+"F0.wireOp",EDGE,"E205");var subQ13=sQuery(id+"F0.wireOp",EDGE,"E212");var subQ14=makeQuery(id+"F1.opExtrude","CAP_FACE",FACE,{"disambiguationData":[OSD([sQuery(id+"F0.wireOp",EDGE,"E204"),subQ11,subQ5,subQ10,subQ4,subQ13,subQ9,subQ3,subQ2,subQ8,subQ7,subQ1])],"isStart":false});var subQ15=makeQuery(id+"F1.opExtrude","SWEPT_FACE",FACE,{"disambiguationData":[OSD([subQ13])]});Q0=makeQuery(id+"F3.hole-3.boolean.opBoolean","SPLIT",FACE,{"disambiguationData":[TD([makeQuery(id+"F3.hole-2.boolean.opBoolean","COPY",FACE,{"derivedFrom":subQ0})])],"derivedFrom":makeQuery(id+"F3.hole-2.boolean.opBoolean","SPLIT",FACE,{"disambiguationData":[TD([subQ15])],"derivedFrom":makeQuery(id+"F3.hole-1.boolean.opBoolean","SPLIT",FACE,{"disambiguationData":[TD([subQ15])],"derivedFrom":makeQuery(id+"F3.hole-0.boolean.opBoolean","SPLIT",FACE,{"disambiguationData":[TD([subQ15])],"derivedFrom":subQ14})})})});}
            extrude(context, id + "F11", {"entities" : qUnion([Q0]), "oppositeDirection" : true, "depth" : 25 * mm, "offsetDistance" : 25 * mm});
        }
        {
            var Q0;
            Q0=sQuery(id+"F2.wireOp",VERTEX,"E443.center");
            var Q1;
            Q1=makeQuery(id+"F1.opExtrude","SWEPT_BODY",BODY,{"disambiguationData":[OSD([sQuery(id+"F0.wireOp",EDGE,"E204"),sQuery(id+"F0.wireOp",EDGE,"E205"),sQuery(id+"F0.wireOp",EDGE,"E207"),sQuery(id+"F0.wireOp",EDGE,"E209"),sQuery(id+"F0.wireOp",EDGE,"E211"),sQuery(id+"F0.wireOp",EDGE,"E212"),sQuery(id+"F0.wireOp",EDGE,"E213"),sQuery(id+"F0.wireOp",EDGE,"E215"),sQuery(id+"F0.wireOp",EDGE,"E216"),sQuery(id+"F0.wireOp",EDGE,"E217"),sQuery(id+"F0.wireOp",EDGE,"E219"),sQuery(id+"F0.wireOp",EDGE,"E220")])]});
            var Q2;
            Q2=makeQuery(id+"F11.opExtrude","SWEPT_BODY",BODY,{"disambiguationData":[OSD([sQuery(id+"F0.wireOp",EDGE,"E204"),sQuery(id+"F0.wireOp",EDGE,"E205"),sQuery(id+"F0.wireOp",EDGE,"E207"),sQuery(id+"F0.wireOp",EDGE,"E209"),sQuery(id+"F0.wireOp",EDGE,"E211"),sQuery(id+"F0.wireOp",EDGE,"E212"),sQuery(id+"F0.wireOp",EDGE,"E213"),sQuery(id+"F0.wireOp",EDGE,"E215"),sQuery(id+"F0.wireOp",EDGE,"E216"),sQuery(id+"F0.wireOp",EDGE,"E217"),sQuery(id+"F0.wireOp",EDGE,"E219"),sQuery(id+"F0.wireOp",EDGE,"E220")])]});
            hole(context, id + "F12", {"style" : HoleStyle.SIMPLE, "endStyle" : HoleEndStyle.BLIND_IN_LAST, "holeDiameter" : 2 * mm, "tapDrillDiameter" : 1.6 * mm, "majorDiameter" : 5 * mm, "holeDepth" : 8 * mm, "tappedDepth" : 12 * mm, "tapClearance" : 3, "locations" : qUnion([Q0]), "scope" : qUnion([Q1, Q2])});
        }
        {
            var Q0;
            Q0=makeQuery(id+"F11.opExtrude","SWEPT_BODY",BODY,{"disambiguationData":[OSD([sQuery(id+"F0.wireOp",EDGE,"E204"),sQuery(id+"F0.wireOp",EDGE,"E205"),sQuery(id+"F0.wireOp",EDGE,"E207"),sQuery(id+"F0.wireOp",EDGE,"E209"),sQuery(id+"F0.wireOp",EDGE,"E211"),sQuery(id+"F0.wireOp",EDGE,"E212"),sQuery(id+"F0.wireOp",EDGE,"E213"),sQuery(id+"F0.wireOp",EDGE,"E215"),sQuery(id+"F0.wireOp",EDGE,"E216"),sQuery(id+"F0.wireOp",EDGE,"E217"),sQuery(id+"F0.wireOp",EDGE,"E219"),sQuery(id+"F0.wireOp",EDGE,"E220")])]});
            deleteBodies(context, id + "F13", {"entities" : qUnion([Q0])});
        }
    });
